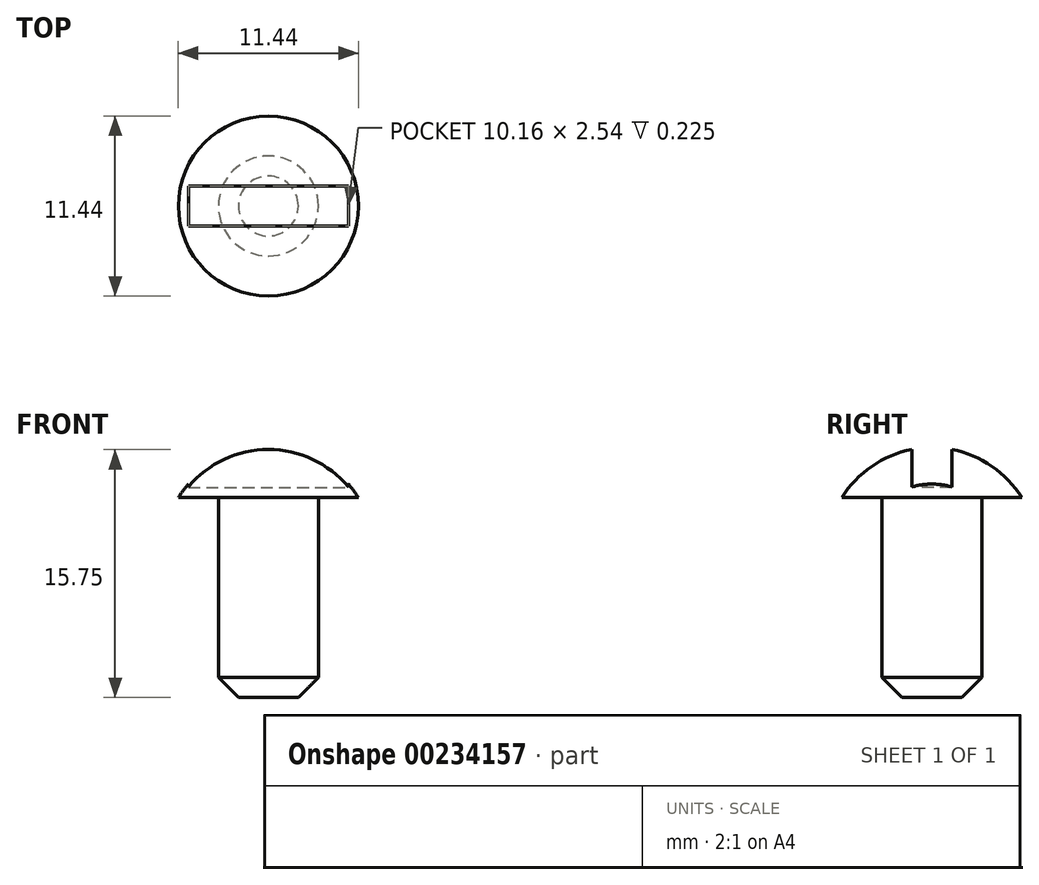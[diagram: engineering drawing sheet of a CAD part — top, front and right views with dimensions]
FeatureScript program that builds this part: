
annotation { "Feature Type Name" : "Feature", "Feature Type Description" : "" }
export const myFeature = defineFeature(function(context is Context, id is Id, definition is map)
    precondition{}
    {
        {
            var Q0;
            Q0=qCreatedBy(makeId("Front.planeOp"),FACE);
            var sketch = newSketch(context, id + "F0", { "sketchPlane" : qUnion([Q0])});
            skLineSegment(sketch, "E0", {"start": v(0, 0) * mm, "end": v(3.18, 0) * mm});
            skLineSegment(sketch, "E1", {"start": v(3.18, 0) * mm, "end": v(3.18, 12.7) * mm});
            skLineSegment(sketch, "E2", {"start": v(3.18, 12.7) * mm, "end": v(5.71, 12.7) * mm});
            skLineSegment(sketch, "E3", {"start": v(0, 0) * mm, "end": v(0, 15.87) * mm});
            skArc(sketch, "E4", {"start": v(5.72, 12.7) * mm, "mid": v(3.27, 15.03) * mm, "end": v(0, 15.87) * mm});
            skLineSegment(sketch, "E5", {"start": v(0, 15.87) * mm, "end": v(0, -2.84) * mm, "construction": true});
            skSolve(sketch);
        }
        {
            var Q0;
            Q0=makeQuery(id+"F0.imprint","IMPRINT",FACE,{"disambiguationData":[TD([[makeQuery(id+"F0.imprint","IMPRINT",EDGE,{"derivedFrom":sQuery(id+"F0.wireOp",EDGE,"E0")}),1.0]])]});
            var Q1;
            Q1=sQuery(id+"F0.wireOp",EDGE,"E5");
            revolve(context, id + "F1", {"entities" : qUnion([Q0]), "axis" : qUnion([Q1]), "revolveType" : RevolveType.FULL});
        }
        {
            var Q0;
            Q0=makeQuery(id+"F1.opRevolve","SWEPT_FACE",FACE,{"disambiguationData":[OSD([sQuery(id+"F0.wireOp",EDGE,"E2")])]});
            cPlane(context, id + "F2", {"entities" : qUnion([Q0]), "cplaneType" : CPlaneType.OFFSET, "offset" : 0.64 * mm, "oppositeDirection" : true, "width" : 152.4 * mm, "height" : 152.4 * mm});
        }
        {
            var Q0;
            Q0=qCreatedBy(id+"F2.planeOp",FACE);
            var sketch = newSketch(context, id + "F3", { "sketchPlane" : qUnion([Q0])});
            skLineSegment(sketch, "E6.bottom", {"start": v(-5.08, -1.27) * mm, "end": v(5.08, -1.27) * mm});
            skLineSegment(sketch, "E6.top", {"start": v(-5.08, 1.27) * mm, "end": v(5.08, 1.27) * mm});
            skLineSegment(sketch, "E6.left", {"start": v(-5.08, -1.27) * mm, "end": v(-5.08, 1.27) * mm});
            skLineSegment(sketch, "E6.right", {"start": v(5.08, -1.27) * mm, "end": v(5.08, 1.27) * mm});
            skPoint(sketch, "E6.middle", {"position": v(0, 0) * mm});
            skSolve(sketch);
        }
        {
            var Q0;
            Q0=qSketchRegion(id+"F3",true);
            extrude(context, id + "F4", {"entities" : qUnion([Q0]), "operationType" : NewBodyOperationType.REMOVE, "endBound" : BoundingType.THROUGH_ALL, "oppositeDirection" : true, "depth" : 25.4 * mm});
        }
        {
            var Q0;
            Q0=makeQuery(id+"F1.opRevolve","SWEPT_EDGE",EDGE,{"disambiguationData":[OSD([sQuery(id+"F0.wireOp",EDGE,"E0"),sQuery(id+"F0.wireOp",EDGE,"E1")])]});
            chamfer(context, id + "F5", {"entities" : qUnion([Q0]), "width" : 1.27 * mm, "tangentPropagation" : true});
        }
    });
